# Revit family: Furniture_Office-Chairs_Flokk_Giroflex-434
name_source: partatom
category: Furniture
units: mm (PartAtom-declared; Revit-internal decimal feet)

## family parameters
Always vertical = Yes
Cut with Voids When Loaded = No
OmniClass Number = 23.40.20.14.14.11
OmniClass Title = Chairs
Room Calculation Point = No
Shared = No
Work Plane-Based = No

## types (1)
- Giroflex 434
    AssetType = Movable
    BIMObjectName = Furniture_Office-Chairs_Flokk_Giroflex-434
    Brand = Flokk
    Category = Giroflex
    Color = Various
    Cost = 0 $
    Default Elevation = 0 mm  [stored 0 ft]
    Description = The giroflex 434 swivel chair impresses with excellent seating comfort and clear styling. The back part of the chair brings the typical Giroflex combination of mesh fabric and formal autonomy to the fore, ergonomically convincing, full of elasticity, transparent and breathable.

The reduction to the bare essentials and the unemotional appearance allow the integration of the chair in any room concept. Fashion statements are also possible, since the mesh backrests can be simply and integrally replaced.

The base cross is made of aluminium or high quality plastic. This version has a low back, height 55 cm, the chair is also available with a medium Back, height 61 cm.
    Designer = Designed by greutmann bolzern designstudio
    DurationUnit = Year
    IfcExportAs = IfcFurnishingElementType
    IfcExportType = CHAIR
    LowestSeatingHeight = 500 mm  [stored 1.64042 ft]
    MainColor = Various
    Manufacturer = Flokk
    ManufacturerName = Flokk
    ManufacturerURL = https://www.flokk.com
    Material = Plastic, Metal and Textile
    Model = Giroflex 434
    ModelNumber = 434-3019
    NBSDescription = Stacking chairs
    NBSReference = 45-35-20/355
    Name = Giroflex-434
    NominalDepth = 675 mm
    NominalLength = 680 mm
    OfficeChairQuaternaryMaterial = Black RAL 9005
    ProductDatasheet = https://flokkplatformprod.blob.core.windows.net
    ProductInformation = The giroflex 434 family impresses users with its excellent ergonomic seating comfort, combined with its clean design.
    SeatingHeight = 500 mm  [stored 1.64042 ft]
    Shape = Sculptured
    Size = 680x675x1015 mm
    URL = https://store.flokk.com
    Uniclass2 = Pr_40_50_12_51
    Uniclass2015Description = Meeting room chairs
    Uniclass2015Reference = Pr_40_50_12_51
    Version = 1
    VersionDate = 10/01/2022
    WarrantyDurationUnit = Year

note: [stored X ft] marks values corroborated as IEEE doubles in the binary element streams (Revit-internal decimal feet)

## geometry (parser evidence)
native form markers: Sweep x5
no freeform markers — native parametric forms only
